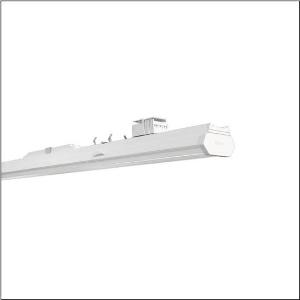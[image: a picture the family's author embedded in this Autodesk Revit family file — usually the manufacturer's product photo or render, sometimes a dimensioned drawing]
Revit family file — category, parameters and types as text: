
# Revit family: licross_r__21_protected_mo_52td1b7n48xg_600d
name_source: partatom
category: Lighting Fixtures
units: mm (PartAtom-declared; Revit-internal decimal feet)

## family parameters
Cut with Voids When Loaded = No
Host = Face
Light Source = No
Part Type = Normal
Room Calculation Point = No
Round Connector Dimension = Use Diameter
Shared = No

## types (1)
- Licross® 21 Protected MO (1 x LED, 8090 lm, 47.9 W, 4000K)
    Apparent Load = 48 VA
    CIE Flux Codes = 54 82 95 97 100
    Color Rendering = 80
    Color Temperature = 4000K
    Default Elevation = 1800 mm
    Description = Licross® 21 Protected MO, luminaire insert, of sheet steel, galvanised, coil coated, white, length: 1.500mm, width: 90mm, height: 103mm, LED rated luminous flux: 8.090lm, light colour: 840, control gear: ON/OFF, with plug, 3-pole, with phase selection, mains connection: 220..240V, AC, 50/60Hz, rated input power: 48W, halogen-free wiring, primary optical cover: cover, of PMMA, light emission: direct distribution, primary light characteristic: symmetric, protection rating (complete): IP54, insulation class (complete): insulation class I (protective earthing), certification: CE, ENEC, VDE, UKCA, protection symbol: D if used in an environment with non-conductive dust loads with corresponding accessories, impact resistance: IK06, permissible ambient temperature for indoor applications: -35..+45°C, corresponds to IFS (International Featured Standards) requirements for safety and quality in the food industry, reducing of maximum allowable ambient temperature of 5°C with ceiling mounting, LABS conformity tested according to VDMA 24364:2018-05, packaging unit: 1 piece
    Height = 92 mm
    Lamp = 1 x LED
    Lamp Light Flux = 8090 lm
    Lamp Power = 47.9 W
    Lamp count = 1
    Length = 1500 mm
    Luminous efficacy = 169 lm/W
    Manufacturer = Siteco
    ModVariant = No
    Model = 52TD1B7N48XG
    Mounting Place = Ceiling
    Mounting Type = Pendant
    Number of Poles = 1
    OnlyDefault = Yes
    Power Factor = 1
    Product Name = Licross® 21 Protected MO
    Product group = luminaire insert
    ProductGroupID = 901
    Protection Class = Protection class I
    Protection Degree = IP 54
    RLX_Detail_Level = 1
    RLX_Emergency_Light_Flux = 0 lm
    RLX_Emergency_Type = 0
    RLX_Emergency_Type_DB = No
    RlxData = <blob elided: 20621 chars, md5=6459d9f3>
    Socket = socket
    Standby Power = 0 W
    System Light Flux = 8090 lm
    System Power = 48 W
    Type Comments = Product without accessories
    Type Image = l_1256148.jpg
    URL = http://relux.com
    VarID = ---
    Voltage = 0 V
    Weight = 0.00 kg
    Width = 88 mm

## geometry (parser evidence)
native form markers: Blend x4, Sweep x11
no freeform markers — native parametric forms only
